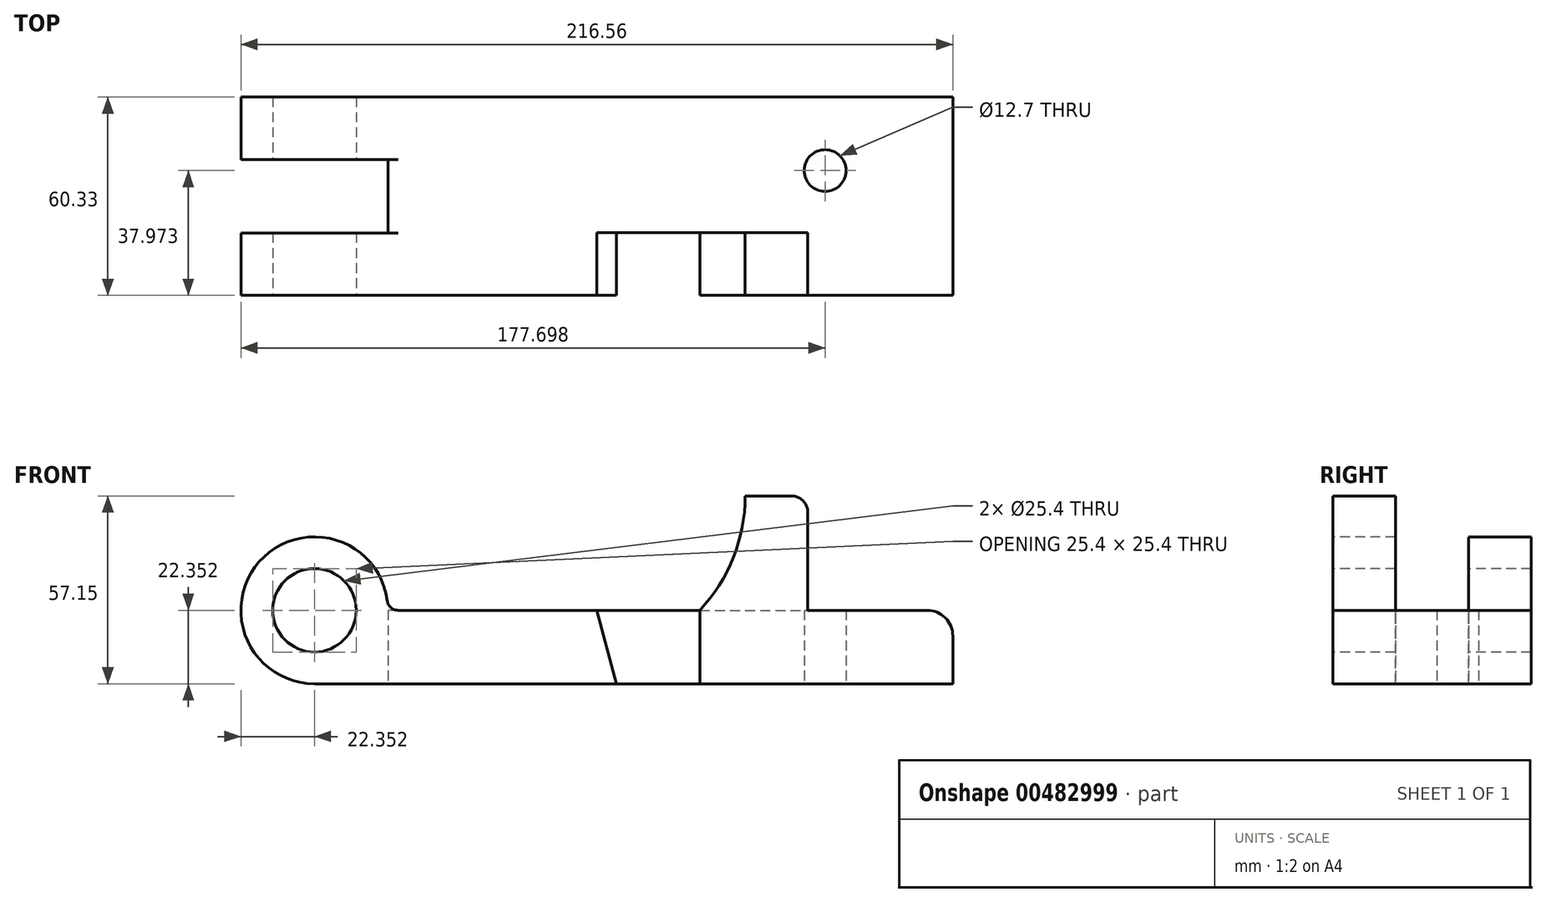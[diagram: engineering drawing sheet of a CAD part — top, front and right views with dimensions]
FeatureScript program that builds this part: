
annotation { "Feature Type Name" : "Feature", "Feature Type Description" : "" }
export const myFeature = defineFeature(function(context is Context, id is Id, definition is map)
    precondition{}
    {
        {
            var Q0;
            Q0=qCreatedBy(makeId("Front.planeOp"),FACE);
            var sketch = newSketch(context, id + "F0", { "sketchPlane" : qUnion([Q0])});
            skLineSegment(sketch, "E0", {"start": v(-102.09, 0) * mm, "end": v(92.12, 0) * mm});
            skLineSegment(sketch, "E1", {"start": v(92.12, 0) * mm, "end": v(92.12, 14.48) * mm});
            skLineSegment(sketch, "E2", {"start": v(84.25, 22.35) * mm, "end": v(48, 22.35) * mm});
            skLineSegment(sketch, "E3", {"start": v(48, 22.35) * mm, "end": v(48, 52.07) * mm});
            skLineSegment(sketch, "E4", {"start": v(42.92, 57.15) * mm, "end": v(28.95, 57.15) * mm});
            skLineSegment(sketch, "E5", {"start": v(15.16, 22.35) * mm, "end": v(-79.74, 22.35) * mm});
            skArc(sketch, "E6", {"start": v(-79.74, 22.35) * mm, "mid": v(-117.9, 38.16) * mm, "end": v(-102.09, 0) * mm});
            skCircle(sketch, "E7", {"center": v(-102.09, 22.35) * mm, "radius": 12.7 * mm});
            skArc(sketch, "E8.filletArc", {"start": v(92.12, 14.48) * mm, "mid": v(89.81, 20.05) * mm, "end": v(84.25, 22.35) * mm});
            skArc(sketch, "E9.filletArc", {"start": v(48, 52.07) * mm, "mid": v(46.51, 55.66) * mm, "end": v(42.92, 57.15) * mm});
            skArc(sketch, "E10", {"start": v(15.16, 22.35) * mm, "mid": v(25.38, 38.43) * mm, "end": v(28.95, 57.15) * mm});
            skSolve(sketch);
        }
        {
            var Q0;
            Q0=makeQuery(id+"F0.imprint","IMPRINT",FACE,{"disambiguationData":[TD([[makeQuery(id+"F0.imprint","IMPRINT",EDGE,{"derivedFrom":sQuery(id+"F0.wireOp",EDGE,"E0")}),1.0]])]});
            extrude(context, id + "F1", {"entities" : qUnion([Q0]), "oppositeDirection" : true, "depth" : 60.32 * mm});
        }
        {
            var Q0;
            Q0=makeQuery(id+"F1.opExtrude","SWEPT_FACE",FACE,{"disambiguationData":[OSD([sQuery(id+"F0.wireOp",EDGE,"E5")])]});
            var sketch = newSketch(context, id + "F2", { "sketchPlane" : qUnion([Q0])});
            skLineSegment(sketch, "E11.0", {"start": v(15.16, 60.33) * mm, "end": v(15.16, 19.05) * mm});
            skLineSegment(sketch, "E12.0", {"start": v(48, 60.33) * mm, "end": v(48, 19.05) * mm});
            skLineSegment(sketch, "E13", {"start": v(15.16, 60.33) * mm, "end": v(48, 60.33) * mm});
            skLineSegment(sketch, "E14", {"start": v(15.16, 19.05) * mm, "end": v(48, 19.05) * mm});
            skSolve(sketch);
        }
        {
            var Q0;
            Q0 = qSketchRegion(id + "F2", true);
            extrude(context, id + "F3", {"entities" : qUnion([Q0]), "operationType" : NewBodyOperationType.REMOVE, "endBound" : BoundingType.UP_TO_NEXT, "depth" : 25.4 * mm});
        }
        {
            var Q0;
            Q0=qCreatedBy(makeId("Front.planeOp"),FACE);
            var sketch = newSketch(context, id + "F4", { "sketchPlane" : qUnion([Q0])});
            skLineSegment(sketch, "E15", {"start": v(15.16, 22.35) * mm, "end": v(15.16, 0) * mm});
            skLineSegment(sketch, "E16", {"start": v(15.16, 0) * mm, "end": v(-10.24, 0) * mm});
            skLineSegment(sketch, "E17", {"start": v(-10.24, 0) * mm, "end": v(-16.24, 22.35) * mm});
            skLineSegment(sketch, "E18", {"start": v(-16.24, 22.35) * mm, "end": v(15.16, 22.35) * mm});
            skCircle(sketch, "E19.0", {"center": v(-102.09, 22.35) * mm, "radius": 12.7 * mm, "construction": true});
            skSolve(sketch);
        }
        {
            var Q0;
            Q0 = qSketchRegion(id + "F4", true);
            extrude(context, id + "F5", {"entities" : qUnion([Q0]), "operationType" : NewBodyOperationType.REMOVE, "oppositeDirection" : true, "depth" : 19.05 * mm});
        }
        {
            var Q0;
            Q0=makeQuery(id+"F3.boolean.opBoolean","MERGE",FACE,{"derivedFrom":[makeQuery(id+"F1.opExtrude","SWEPT_FACE",FACE,{"disambiguationData":[OSD([sQuery(id+"F0.wireOp",EDGE,"E2")])]}),makeQuery(id+"F1.opExtrude","SWEPT_FACE",FACE,{"disambiguationData":[OSD([sQuery(id+"F0.wireOp",EDGE,"E5")])]}),makeQuery(id+"F3.opExtrude","CAP_FACE",FACE,{"disambiguationData":[OSD([sQuery(id+"F2.wireOp",EDGE,"E11.0"),sQuery(id+"F2.wireOp",EDGE,"E12.0"),sQuery(id+"F2.wireOp",EDGE,"E13"),sQuery(id+"F2.wireOp",EDGE,"E14")])],"isStart":true})]});
            var sketch = newSketch(context, id + "F6", { "sketchPlane" : qUnion([Q0])});
            skLineSegment(sketch, "E20.0", {"start": v(-79.74, 41.33) * mm, "end": v(-79.74, 19) * mm});
            skCircle(sketch, "E21", {"center": v(53.26, 37.97) * mm, "radius": 6.35 * mm});
            skLineSegment(sketch, "E22", {"start": v(-130.19, 41.33) * mm, "end": v(-130.19, 19) * mm});
            skLineSegment(sketch, "E23", {"start": v(-130.19, 41.33) * mm, "end": v(-79.74, 41.33) * mm});
            skLineSegment(sketch, "E24", {"start": v(-130.19, 19) * mm, "end": v(-79.74, 19) * mm});
            skSolve(sketch);
        }
        {
            var Q0;
            Q0 = qSketchRegion(id + "F6", true);
            extrude(context, id + "F7", {"entities" : qUnion([Q0]), "operationType" : NewBodyOperationType.REMOVE, "endBound" : BoundingType.SYMMETRIC, "depth" : 95 * mm});
        }
        {
            var Q0;
            {var subQ0=sQuery(id+"F0.wireOp",EDGE,"E6");var subQ1=makeQuery(id+"F1.opExtrude","SWEPT_FACE",FACE,{"disambiguationData":[OSD([subQ0])]});var subQ2=sQuery(id+"F0.wireOp",EDGE,"E5");var subQ3=makeQuery(id+"F1.opExtrude","SWEPT_FACE",FACE,{"disambiguationData":[OSD([subQ2])]});var subQ4=sQuery(id+"F0.wireOp",EDGE,"E2");var subQ5=makeQuery(id+"F1.opExtrude","SWEPT_FACE",FACE,{"disambiguationData":[OSD([subQ4])]});var subQ6=makeQuery(id+"F3.opExtrude","CAP_FACE",FACE,{"disambiguationData":[OSD([sQuery(id+"F2.wireOp",EDGE,"E11.0"),sQuery(id+"F2.wireOp",EDGE,"E12.0"),sQuery(id+"F2.wireOp",EDGE,"E13"),sQuery(id+"F2.wireOp",EDGE,"E14")])],"isStart":true});Q0=makeQuery(id+"F7.boolean.opBoolean","SPLIT",EDGE,{"disambiguationData":[topologyDisambiguationEdgeConnected([subQ5,subQ3,subQ1,subQ6]),TD([makeQuery(id+"F7.opExtrude","SWEPT_FACE",FACE,{"disambiguationData":[OSD([sQuery(id+"F6.wireOp",EDGE,"E24")])]})])],"derivedFrom":makeQuery(id+"F1.opExtrude","SWEPT_EDGE",EDGE,{"disambiguationData":[OSD([subQ2,subQ0])]})});}
            var Q1;
            {var subQ0=sQuery(id+"F0.wireOp",EDGE,"E6");var subQ1=makeQuery(id+"F1.opExtrude","SWEPT_FACE",FACE,{"disambiguationData":[OSD([subQ0])]});var subQ2=sQuery(id+"F0.wireOp",EDGE,"E2");var subQ3=makeQuery(id+"F1.opExtrude","SWEPT_FACE",FACE,{"disambiguationData":[OSD([subQ2])]});var subQ4=makeQuery(id+"F3.opExtrude","CAP_FACE",FACE,{"disambiguationData":[OSD([sQuery(id+"F2.wireOp",EDGE,"E11.0"),sQuery(id+"F2.wireOp",EDGE,"E12.0"),sQuery(id+"F2.wireOp",EDGE,"E13"),sQuery(id+"F2.wireOp",EDGE,"E14")])],"isStart":true});var subQ5=sQuery(id+"F0.wireOp",EDGE,"E5");var subQ6=makeQuery(id+"F1.opExtrude","SWEPT_FACE",FACE,{"disambiguationData":[OSD([subQ5])]});Q1=makeQuery(id+"F7.boolean.opBoolean","SPLIT",EDGE,{"disambiguationData":[topologyDisambiguationEdgeConnected([subQ3,subQ6,subQ1,subQ4]),TD([makeQuery(id+"F7.opExtrude","SWEPT_FACE",FACE,{"disambiguationData":[OSD([sQuery(id+"F6.wireOp",EDGE,"E23")])]})])],"derivedFrom":makeQuery(id+"F1.opExtrude","SWEPT_EDGE",EDGE,{"disambiguationData":[OSD([subQ5,subQ0])]})});}
            fillet(context, id + "F8", {"entities" : qUnion([Q0, Q1]), "radius" : 3.3 * mm, "tangentPropagation" : true, "allowEdgeOverflow" : false});
        }
    });
